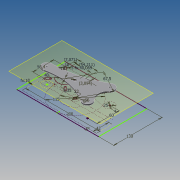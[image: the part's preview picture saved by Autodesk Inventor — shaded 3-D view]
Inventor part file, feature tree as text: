
AUTODESK INVENTOR PART (.ipt)
format: ipt  version: 2017 (Build 210142000, 142)  size: 148,992 bytes
history: native  units: mm
features: other x5, sketch x2, plane x1, extrude x1, reference x1
ambient origin geometry x8: Origin, YZ Plane, XZ Plane, XY Plane, X Axis, Y Axis, Z Axis, Center Point
bodies: Body1 (feature_tree)
feature tree (10):
  other  "Sólido1"
  sketch  "Boceto1"  dims[d0=6.35mm d1=56.4mm]
  plane  "Plano de trabajo1"
  extrude  "Extrusión1"  Depth=56.4mm
  sketch  "Boceto2"  dims[d2=67.5mm d3=40.0mm d4=200.0mm d5=42.0mm d6=8.0mm d7=3.094466mm d8=5.0mm d9=40.068932mm d10=10.0mm d11=54.211068mm d12=7.071068mm d13=4.0mm d14=115.0mm d15=25.0mm d16=60.0mm d17=60.0mm d18=5.0mm d19=10.0mm d20=22.0mm d21=130.0mm d22=10.0mm d23=38.0mm d24=4.0mm d25=0.0mm]
  reference  "Referencia1"
  other  "<userpath>\Dropbox\E\Caja Motriz\transmision Engranajes.iam"
  other  "transmision Engranajes.iam"
  other  "Plato Carrete:1"
  other  "carrete:1"
